# Revit family: Ginko 2.2
name_source: partatom
category: Lighting Fixtures
revit_build: Autodesk Revit 2017 (Build: 20160225_1515(x64)
units: mm (PartAtom-declared; Revit-internal decimal feet)

## family parameters
Always vertical = No
Cut with Voids When Loaded = No
Light Source = No
OmniClass Number = 23.80.70.00
OmniClass Title = Lighting
Part Type = Normal
Room Calculation Point = No
Round Connector Dimension = Use Diameter
Shared = No
Work Plane-Based = Yes

## types (5) — shared parameters
Apparent Load Phase 1 = 5 W
Base = L&L_White
Base bracket = Ginko2.0_Base bracket
Bracket = L&L_Stainless steel
CRI = -
Code = GN2232 6 I Stainless steel; GN2232 6 E White; GN2232 6 N Black anodized; GN2232 6 F Grey; GN2232 6 H Anthracite; GN2232 6 T Cor-ten; GN2232 6 5 Jasper green
Control system = -
Cutout dimensions = -
Default Elevation = 1219 mm
Delivered lumen output = 191 lm; 70 lm (R); 90 lm (G); 31 lm (B)
Description = Outdoor projectors
Energy efficiency class = A A+ A++
Features = -
Geometry = Ginko2.2_mod : Ginko_2.0
H1 = 55 mm  [stored 0.180446 ft]
Height mm = 107 mm  [stored 0.35105 ft]
IP = 66
LED Colour = RGB
Length mm = 58 mm  [stored 0.190289 ft]
Lens = L&L_Lens
Lumen output at source = 253 lm; 82 lm (R); 114 lm (G); 57 lm (B)
Manufacturer = L&L Luce&Light
Material = body in AISI 316L stainless steel or anticorodal aluminium, AISI 316L stainless steel bracket, screen in tempered, transparent extra-clear glass
Middle = L&L_White
Model = Ginko 2.2
Mounting = surface mounted (ceiling, wall, ground, spike)
No. and type of led = 3 power LEDs; 50000h L90 B10  (Ta 25°C)
Notes = -
Power = 5W
Power cables = includes 1,5 m FEP+RUB cable (equivalent to H05RN-F cable) 6x0,50/0,50 Ø6,3 mm
Power supply = 500mA
Power supply unit = not included
Top = L&L_White
URL = https://www.lucelight.it
URL Accessories and power supply units = https://www.lucelight.it
URL Catalogue = https://www.lucelight.it
URL DXF = https://www.lucelight.it
URL Description = https://www.lucelight.it
URL General code = https://www.lucelight.it
URL IES Photometric file = https://www.lucelight.it
URL Image = https://www.lucelight.it
URL Technical sheet = https://www.lucelight.it
Vertical rotation max = 190.00°
Voltage = 0 V
Weight kg = 0.38
Width mm = 54 mm  [stored 0.177165 ft]
Wiring = series
X1 = 100 mm  [stored 0.328084 ft]

## per-type parameters (varying)
| type | Light Source | Optics |
| Ginko 2.2_L 45° (RGB 5W 3x500mA) | Light Source_2.2 : L45° | 45° |
| Ginko 2.2_M 34° (RGB 5W 3x500mA) | Light Source_2.2 : M34° | 34° |
| Ginko 2.2_S 20° (RGB 5W 3x500mA) | Light Source_2.2 : S20° | 20° |
| Ginko 2.2_W 21°x42° (RGB 5W 3x500mA) | Light Source_2.2 : W21°x42° | 21°x42° |
| Ginko 2.2_X 42°x21° (RGB 5W 3x500mA) | Light Source_2.2 : X42°x21° | 42°x21° |

note: [stored X ft] marks values corroborated as IEEE doubles in the binary element streams (Revit-internal decimal feet)

## geometry (parser evidence)
native form markers: Blend x2, Sweep x9
no freeform markers — native parametric forms only
